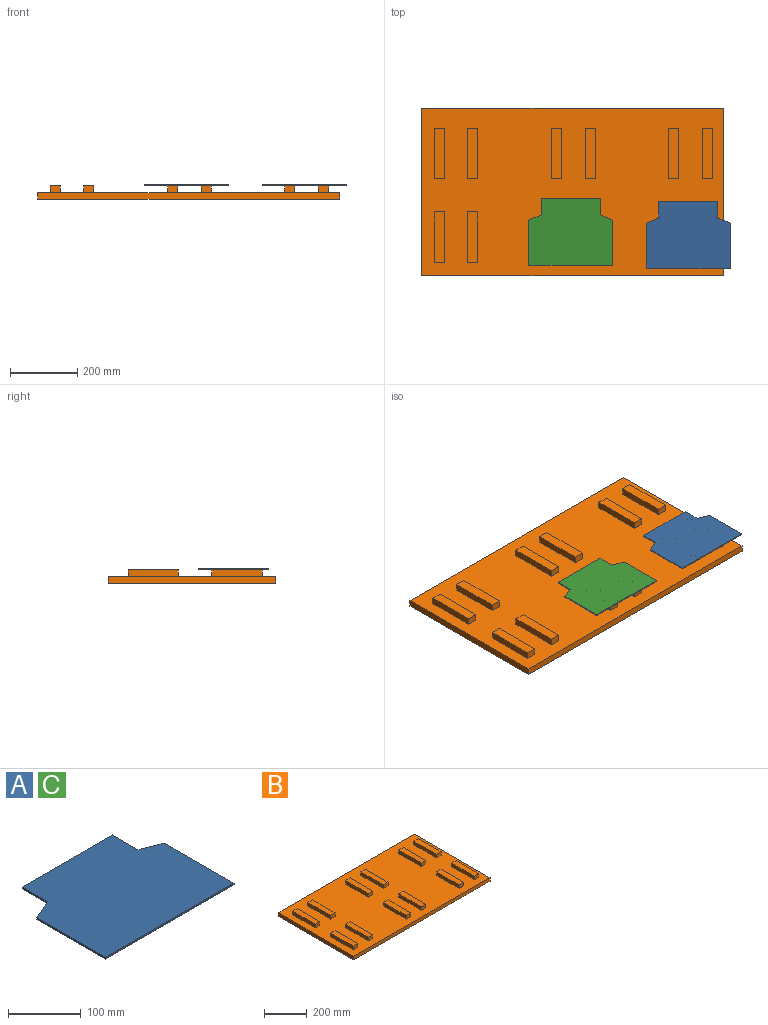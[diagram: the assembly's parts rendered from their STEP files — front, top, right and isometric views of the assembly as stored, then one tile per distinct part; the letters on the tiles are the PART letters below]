
ASSEMBLY  parts=3 mates=2
PART A: 10 faces, bbox 250x200x3 mm
  f0: plane 37.08x15mm, normal (0.37,0.93,0), area 120mm2, adj f1,f7,f8,f9
  f1: plane 50x3mm, normal (1,0,0), area 150mm2, adj f0,f2,f8,f9
  f2: plane 175.99x3mm, normal (0,1,0), area 528mm2, adj f1,f3,f8,f9
  f3: plane 50x3mm, normal (-1,0,0), area 150mm2, adj f2,f4,f8,f9
  f4: plane 36.93x15.37mm, normal (-0.38,0.92,0), area 120mm2, adj f3,f5,f8,f9
  f5: plane 134.63x3mm, normal (-1,0,0), area 403.9mm2, adj f4,f6,f8,f9
  f6: plane 250x3mm, normal (0,-1,0), area 750mm2, adj f5,f7,f8,f9
  f7: plane 135x3mm, normal (1,0,0), area 405mm2, adj f0,f6,f8,f9
  f8: plane 250x200mm, normal (0,0,1), area 45737.6mm2, adj f0,f1,f2,f3,f4,f5,f6,f7
  f9: plane 250x200mm, normal (0,0,-1), area 45737.6mm2, adj f0,f1,f2,f3,f4,f5,f6,f7
PART B: 66 faces, bbox 900x500x40 mm
  f0: plane 150x20mm, normal (1,0,0), area 3000mm2, adj f1,f3,f4,f30
  f1: plane 30x20mm, normal (0,1,0), area 600mm2, adj f0,f2,f4,f30
  f2: plane 150x20mm, normal (-1,0,0), area 3000mm2, adj f1,f3,f4,f30
  f3: plane 30x20mm, normal (0,-1,0), area 600mm2, adj f0,f2,f4,f30
  f4: plane 150x30mm, normal (0,0,1), area 4500mm2, adj f0,f1,f2,f3
  f5: plane 150x20mm, normal (1,0,0), area 3000mm2, adj f6,f8,f9,f30
  f6: plane 30x20mm, normal (0,1,0), area 600mm2, adj f5,f7,f9,f30
  f7: plane 150x20mm, normal (-1,0,0), area 3000mm2, adj f6,f8,f9,f30
  f8: plane 30x20mm, normal (0,-1,0), area 600mm2, adj f5,f7,f9,f30
  f9: plane 150x30mm, normal (0,0,1), area 4500mm2, adj f5,f6,f7,f8
  f10: plane 150x20mm, normal (1,0,0), area 3000mm2, adj f11,f13,f14,f30
  f11: plane 30x20mm, normal (0,1,0), area 600mm2, adj f10,f12,f14,f30
  f12: plane 150x20mm, normal (-1,0,0), area 3000mm2, adj f11,f13,f14,f30
  f13: plane 30x20mm, normal (0,-1,0), area 600mm2, adj f10,f12,f14,f30
  f14: plane 150x30mm, normal (0,0,1), area 4500mm2, adj f10,f11,f12,f13
  f15: plane 150x20mm, normal (1,0,0), area 3000mm2, adj f16,f18,f19,f30
  f16: plane 30x20mm, normal (0,1,0), area 600mm2, adj f15,f17,f19,f30
  f17: plane 150x20mm, normal (-1,0,0), area 3000mm2, adj f16,f18,f19,f30
  f18: plane 30x20mm, normal (0,-1,0), area 600mm2, adj f15,f17,f19,f30
  f19: plane 150x30mm, normal (0,0,1), area 4500mm2, adj f15,f16,f17,f18
  f20: plane 150x20mm, normal (1,0,0), area 3000mm2, adj f21,f23,f24,f30
  f21: plane 30x20mm, normal (0,1,0), area 600mm2, adj f20,f22,f24,f30
  f22: plane 150x20mm, normal (-1,0,0), area 3000mm2, adj f21,f23,f24,f30
  f23: plane 30x20mm, normal (0,-1,0), area 600mm2, adj f20,f22,f24,f30
  f24: plane 150x30mm, normal (0,0,1), area 4500mm2, adj f20,f21,f22,f23
  f25: plane 150x20mm, normal (1,0,0), area 3000mm2, adj f26,f28,f29,f30
  f26: plane 30x20mm, normal (0,1,0), area 600mm2, adj f25,f27,f29,f30
  f27: plane 150x20mm, normal (-1,0,0), area 3000mm2, adj f26,f28,f29,f30
  f28: plane 30x20mm, normal (0,-1,0), area 600mm2, adj f25,f27,f29,f30
  f29: plane 150x30mm, normal (0,0,1), area 4500mm2, adj f25,f26,f27,f28
  f30: plane 900x500mm, normal (0,0,1), area 396000mm2, adj f0,f1,f2,f3,f5,f6,f7,f8
  f31: plane 500x20mm, normal (1,0,0), area 10000mm2, adj f30,f32,f34,f35
  f32: plane 900x20mm, normal (0,1,0), area 18000mm2, adj f30,f31,f33,f35
  f33: plane 500x20mm, normal (-1,0,0), area 10000mm2, adj f30,f32,f34,f35
  f34: plane 900x20mm, normal (0,-1,0), area 18000mm2, adj f30,f31,f33,f35
  f35: plane 900x500mm, normal (0,0,-1), area 450000mm2, adj f31,f32,f33,f34
  f36: plane 150x20mm, normal (1,0,0), area 3000mm2, adj f30,f37,f39,f40
  f37: plane 30x20mm, normal (0,1,0), area 600mm2, adj f30,f36,f38,f40
  f38: plane 150x20mm, normal (-1,0,0), area 3000mm2, adj f30,f37,f39,f40
  f39: plane 30x20mm, normal (0,-1,0), area 600mm2, adj f30,f36,f38,f40
  f40: plane 150x30mm, normal (0,0,1), area 4500mm2, adj f36,f37,f38,f39
  f41: plane 150x20mm, normal (1,0,0), area 3000mm2, adj f30,f42,f44,f45
  f42: plane 30x20mm, normal (0,1,0), area 600mm2, adj f30,f41,f43,f45
  f43: plane 150x20mm, normal (-1,0,0), area 3000mm2, adj f30,f42,f44,f45
  f44: plane 30x20mm, normal (0,-1,0), area 600mm2, adj f30,f41,f43,f45
  f45: plane 150x30mm, normal (0,0,1), area 4500mm2, adj f41,f42,f43,f44
  f46: plane 150x20mm, normal (1,0,0), area 3000mm2, adj f30,f47,f49,f50
  f47: plane 30x20mm, normal (0,1,0), area 600mm2, adj f30,f46,f48,f50
  f48: plane 150x20mm, normal (-1,0,0), area 3000mm2, adj f30,f47,f49,f50
  f49: plane 30x20mm, normal (0,-1,0), area 600mm2, adj f30,f46,f48,f50
  f50: plane 150x30mm, normal (0,0,1), area 4500mm2, adj f46,f47,f48,f49
  f51: plane 150x20mm, normal (1,0,0), area 3000mm2, adj f30,f52,f54,f55
  f52: plane 30x20mm, normal (0,1,0), area 600mm2, adj f30,f51,f53,f55
  f53: plane 150x20mm, normal (-1,0,0), area 3000mm2, adj f30,f52,f54,f55
  f54: plane 30x20mm, normal (0,-1,0), area 600mm2, adj f30,f51,f53,f55
  f55: plane 150x30mm, normal (0,0,1), area 4500mm2, adj f51,f52,f53,f54
  f56: plane 150x20mm, normal (1,0,0), area 3000mm2, adj f30,f57,f59,f60
  f57: plane 30x20mm, normal (0,1,0), area 600mm2, adj f30,f56,f58,f60
  f58: plane 150x20mm, normal (-1,0,0), area 3000mm2, adj f30,f57,f59,f60
  f59: plane 30x20mm, normal (0,-1,0), area 600mm2, adj f30,f56,f58,f60
  f60: plane 150x30mm, normal (0,0,1), area 4500mm2, adj f56,f57,f58,f59
  f61: plane 150x20mm, normal (1,0,0), area 3000mm2, adj f30,f62,f64,f65
  f62: plane 30x20mm, normal (0,1,0), area 600mm2, adj f30,f61,f63,f65
  f63: plane 150x20mm, normal (-1,0,0), area 3000mm2, adj f30,f62,f64,f65
  f64: plane 30x20mm, normal (0,-1,0), area 600mm2, adj f30,f61,f63,f65
  f65: plane 150x30mm, normal (0,0,1), area 4500mm2, adj f61,f62,f63,f64
PART C: same geometry as A
PLACE A t=(-34.76,-362.28,39.29)mm
PLACE B t=(-281.39,-9.24,-0.71)mm
PLACE C t=(-385.68,-352.9,39.29)mm
MATE planar C.f9 <-> B.f50  axis (0,0,-1) through (-260.76,-152.9,39.29)mm
MATE planar A.f9 <-> B.f65  axis (0,0,-1) through (90.24,-268.9,39.29)mm
